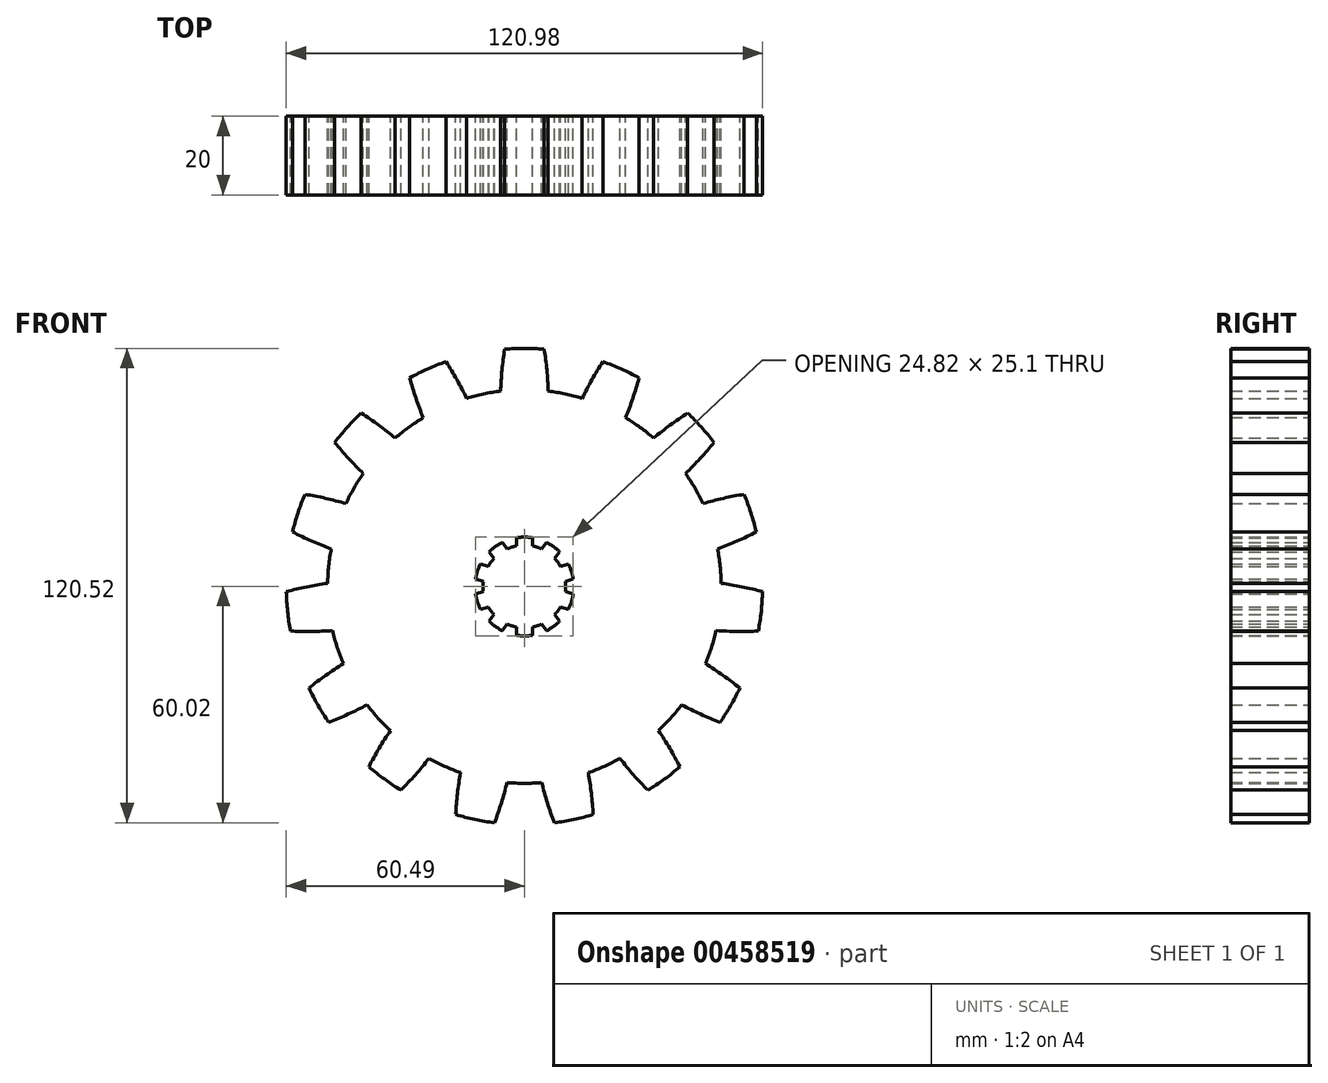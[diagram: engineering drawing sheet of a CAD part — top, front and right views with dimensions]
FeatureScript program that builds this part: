
annotation { "Feature Type Name" : "Feature", "Feature Type Description" : "" }
export const myFeature = defineFeature(function(context is Context, id is Id, definition is map)
    precondition{}
    {
        {
            var Q0;
            Q0=qCreatedBy(makeId("Front.planeOp"),FACE);
            var sketch = newSketch(context, id + "F0", { "sketchPlane" : qUnion([Q0])});
            skCircle(sketch, "E0", {"center": v(0, 0) * mm, "radius": 10.5 * mm});
            skLineSegment(sketch, "E1.left", {"start": v(2.05, -12.38) * mm, "end": v(2.05, -10.3) * mm});
            skLineSegment(sketch, "E1.right", {"start": v(-2.05, -12.38) * mm, "end": v(-2.05, -10.3) * mm});
            skLineSegment(sketch, "E2.1.0", {"start": v(8.94, -8.81) * mm, "end": v(7.71, -7.13) * mm});
            skLineSegment(sketch, "E2.1.1", {"start": v(5.62, -11.22) * mm, "end": v(4.4, -9.54) * mm});
            skLineSegment(sketch, "E2.2.0", {"start": v(12.4, -1.88) * mm, "end": v(10.43, -1.23) * mm});
            skLineSegment(sketch, "E2.2.1", {"start": v(11.14, -5.78) * mm, "end": v(9.16, -5.13) * mm});
            skLineSegment(sketch, "E2.3.0", {"start": v(11.14, 5.78) * mm, "end": v(9.16, 5.13) * mm});
            skLineSegment(sketch, "E2.3.1", {"start": v(12.4, 1.88) * mm, "end": v(10.43, 1.23) * mm});
            skLineSegment(sketch, "E2.4.0", {"start": v(5.62, 11.22) * mm, "end": v(4.4, 9.54) * mm});
            skLineSegment(sketch, "E2.4.1", {"start": v(8.94, 8.81) * mm, "end": v(7.71, 7.13) * mm});
            skLineSegment(sketch, "E2.5.0", {"start": v(-2.05, 12.38) * mm, "end": v(-2.05, 10.3) * mm});
            skLineSegment(sketch, "E2.5.1", {"start": v(2.05, 12.38) * mm, "end": v(2.05, 10.3) * mm});
            skLineSegment(sketch, "E2.6.0", {"start": v(-8.94, 8.81) * mm, "end": v(-7.71, 7.13) * mm});
            skLineSegment(sketch, "E2.6.1", {"start": v(-5.62, 11.22) * mm, "end": v(-4.4, 9.54) * mm});
            skLineSegment(sketch, "E2.7.0", {"start": v(-12.4, 1.88) * mm, "end": v(-10.43, 1.23) * mm});
            skLineSegment(sketch, "E2.7.1", {"start": v(-11.14, 5.78) * mm, "end": v(-9.16, 5.13) * mm});
            skLineSegment(sketch, "E2.8.0", {"start": v(-11.14, -5.78) * mm, "end": v(-9.16, -5.13) * mm});
            skLineSegment(sketch, "E2.9.0", {"start": v(-5.62, -11.22) * mm, "end": v(-4.4, -9.54) * mm});
            skLineSegment(sketch, "E2.9.1", {"start": v(-8.94, -8.81) * mm, "end": v(-7.71, -7.13) * mm});
            skLineSegment(sketch, "E3.trimOffspring", {"start": v(4.4, 9.54) * mm, "end": v(5.62, 11.22) * mm});
            skLineSegment(sketch, "E4.trimOffspring", {"start": v(2.05, 10.3) * mm, "end": v(2.05, 12.38) * mm});
            skLineSegment(sketch, "E5.trimOffspring", {"start": v(-4.4, 9.54) * mm, "end": v(-5.62, 11.22) * mm});
            skLineSegment(sketch, "E6.trimOffspring", {"start": v(-7.71, 7.13) * mm, "end": v(-8.94, 8.81) * mm});
            skLineSegment(sketch, "E7.trimOffspring", {"start": v(-10.43, 1.23) * mm, "end": v(-12.4, 1.88) * mm});
            skLineSegment(sketch, "E8.trimOffspring", {"start": v(-4.4, -9.54) * mm, "end": v(-5.62, -11.22) * mm});
            skLineSegment(sketch, "E9.trimOffspring", {"start": v(10.43, 1.23) * mm, "end": v(12.4, 1.88) * mm});
            skLineSegment(sketch, "E10.trimOffspring", {"start": v(9.16, 5.13) * mm, "end": v(11.14, 5.78) * mm});
            skLineSegment(sketch, "E11.trimOffspring", {"start": v(-2.05, 10.3) * mm, "end": v(-2.05, 12.38) * mm});
            skLineSegment(sketch, "E12.trimOffspring", {"start": v(-9.16, 5.13) * mm, "end": v(-11.14, 5.78) * mm});
            skLineSegment(sketch, "E13.trimOffspring", {"start": v(-10.43, -1.23) * mm, "end": v(-12.4, -1.88) * mm});
            skLineSegment(sketch, "E14.trimOffspring", {"start": v(-9.16, -5.13) * mm, "end": v(-11.14, -5.78) * mm});
            skLineSegment(sketch, "E15.trimOffspring", {"start": v(-7.71, -7.13) * mm, "end": v(-8.94, -8.81) * mm});
            skLineSegment(sketch, "E16.trimOffspring", {"start": v(-2.05, -10.3) * mm, "end": v(-2.05, -12.38) * mm});
            skLineSegment(sketch, "E17.trimOffspring", {"start": v(4.4, -9.54) * mm, "end": v(5.62, -11.22) * mm});
            skLineSegment(sketch, "E18.trimOffspring", {"start": v(7.71, 7.13) * mm, "end": v(8.94, 8.81) * mm});
            skLineSegment(sketch, "E19.trimOffspring", {"start": v(10.43, -1.23) * mm, "end": v(12.4, -1.88) * mm});
            skLineSegment(sketch, "E20.trimOffspring", {"start": v(9.16, -5.13) * mm, "end": v(11.14, -5.78) * mm});
            skLineSegment(sketch, "E21.trimOffspring", {"start": v(7.71, -7.13) * mm, "end": v(8.94, -8.81) * mm});
            skLineSegment(sketch, "E22.trimOffspring", {"start": v(2.05, -10.3) * mm, "end": v(2.05, -12.38) * mm});
            skArc(sketch, "E23", {"start": v(-5.62, 11.22) * mm, "mid": v(-7.38, 10.15) * mm, "end": v(-8.94, 8.81) * mm});
            skPoint(sketch, "E24.orphan", {"position": v(-2.05, 12.55) * mm});
            skPoint(sketch, "E25.orphan", {"position": v(2.05, 12.55) * mm});
            skPoint(sketch, "E26.orphan", {"position": v(-5.72, 11.36) * mm});
            skPoint(sketch, "E27.orphan", {"position": v(-9.04, 8.95) * mm});
            skPoint(sketch, "E28.orphan", {"position": v(5.72, 11.36) * mm});
            skPoint(sketch, "E29.orphan", {"position": v(9.04, 8.95) * mm});
            skPoint(sketch, "E30.orphan", {"position": v(11.3, 5.83) * mm});
            skPoint(sketch, "E31.orphan", {"position": v(12.57, 1.93) * mm});
            skPoint(sketch, "E32.orphan", {"position": v(12.57, -1.93) * mm});
            skPoint(sketch, "E33.orphan", {"position": v(11.3, -5.83) * mm});
            skPoint(sketch, "E34.orphan", {"position": v(9.04, -8.95) * mm});
            skPoint(sketch, "E35.orphan", {"position": v(5.72, -11.36) * mm});
            skPoint(sketch, "E36.orphan", {"position": v(2.05, -12.55) * mm});
            skPoint(sketch, "E37.orphan", {"position": v(-2.05, -12.55) * mm});
            skPoint(sketch, "E38.orphan", {"position": v(-5.72, -11.36) * mm});
            skPoint(sketch, "E39.orphan", {"position": v(-9.04, -8.95) * mm});
            skPoint(sketch, "E40.orphan", {"position": v(-11.3, -5.83) * mm});
            skPoint(sketch, "E41.orphan", {"position": v(-12.57, -1.93) * mm});
            skPoint(sketch, "E42.orphan", {"position": v(-12.57, 1.93) * mm});
            skPoint(sketch, "E43.orphan", {"position": v(-11.3, 5.83) * mm});
            skArc(sketch, "E44.trimOffspring", {"start": v(2.05, 12.38) * mm, "mid": v(0, 12.55) * mm, "end": v(-2.05, 12.38) * mm});
            skArc(sketch, "E45.trimOffspring", {"start": v(8.94, 8.81) * mm, "mid": v(7.38, 10.15) * mm, "end": v(5.62, 11.22) * mm});
            skArc(sketch, "E46.trimOffspring", {"start": v(-11.14, 5.78) * mm, "mid": v(-11.94, 3.88) * mm, "end": v(-12.4, 1.88) * mm});
            skArc(sketch, "E47.trimOffspring", {"start": v(-12.4, -1.88) * mm, "mid": v(-11.94, -3.88) * mm, "end": v(-11.14, -5.78) * mm});
            skArc(sketch, "E48.trimOffspring", {"start": v(-8.94, -8.81) * mm, "mid": v(-7.38, -10.15) * mm, "end": v(-5.62, -11.22) * mm});
            skArc(sketch, "E49.trimOffspring", {"start": v(-2.05, -12.38) * mm, "mid": v(0, -12.55) * mm, "end": v(2.05, -12.38) * mm});
            skArc(sketch, "E50.trimOffspring", {"start": v(5.62, -11.22) * mm, "mid": v(7.38, -10.15) * mm, "end": v(8.94, -8.81) * mm});
            skArc(sketch, "E51.trimOffspring", {"start": v(11.14, -5.78) * mm, "mid": v(11.94, -3.88) * mm, "end": v(12.4, -1.88) * mm});
            skArc(sketch, "E52.trimOffspring", {"start": v(12.4, 1.88) * mm, "mid": v(11.94, 3.88) * mm, "end": v(11.14, 5.78) * mm});
            skSolve(sketch);
        }
        {
            var Q0;
            Q0=qCreatedBy(makeId("Front.planeOp"),FACE);
            var sketch = newSketch(context, id + "F1", { "sketchPlane" : qUnion([Q0])});
            skCircle(sketch, "E53", {"center": v(0, 0) * mm, "radius": 50 * mm});
            skArc(sketch, "E54", {"start": v(-5.04, 60.29) * mm, "mid": v(-5.7, 54.98) * mm, "end": v(-6.05, 49.63) * mm});
            skArc(sketch, "E55.MirrorC", {"start": v(5.04, 60.29) * mm, "mid": v(5.7, 54.98) * mm, "end": v(6.05, 49.63) * mm});
            skArc(sketch, "E56.trimOffspring", {"start": v(5.04, 60.29) * mm, "mid": v(0, 60.5) * mm, "end": v(-5.04, 60.29) * mm});
            skArc(sketch, "E57.1.0", {"start": v(-29.12, 53.03) * mm, "mid": v(-27.57, 47.9) * mm, "end": v(-25.71, 42.88) * mm});
            skArc(sketch, "E57.1.1", {"start": v(-19.92, 57.13) * mm, "mid": v(-24.6, 55.27) * mm, "end": v(-29.12, 53.03) * mm});
            skArc(sketch, "E57.1.2", {"start": v(-19.92, 57.13) * mm, "mid": v(-17.15, 52.54) * mm, "end": v(-14.66, 47.8) * mm});
            skArc(sketch, "E57.2.0", {"start": v(-48.17, 36.6) * mm, "mid": v(-44.67, 32.55) * mm, "end": v(-40.93, 28.72) * mm});
            skArc(sketch, "E57.2.1", {"start": v(-41.43, 44.09) * mm, "mid": v(-44.96, 40.48) * mm, "end": v(-48.17, 36.6) * mm});
            skArc(sketch, "E57.2.2", {"start": v(-41.43, 44.09) * mm, "mid": v(-37.04, 41.02) * mm, "end": v(-32.84, 37.7) * mm});
            skArc(sketch, "E58.3.3.0", {"start": v(-58.9, 13.84) * mm, "mid": v(-54.05, 11.57) * mm, "end": v(-49.07, 9.59) * mm});
            skArc(sketch, "E58.4.3.0", {"start": v(-55.78, 23.42) * mm, "mid": v(-57.54, 18.7) * mm, "end": v(-58.9, 13.84) * mm});
            skArc(sketch, "E58.8.3.0", {"start": v(-55.78, 23.42) * mm, "mid": v(-50.52, 22.4) * mm, "end": v(-45.34, 21.09) * mm});
            skArc(sketch, "E58.3.4.0", {"start": v(-59.43, -11.31) * mm, "mid": v(-54.08, -11.42) * mm, "end": v(-48.73, -11.2) * mm});
            skArc(sketch, "E58.4.4.0", {"start": v(-60.49, -1.3) * mm, "mid": v(-60.17, -6.32) * mm, "end": v(-59.43, -11.31) * mm});
            skArc(sketch, "E58.8.4.0", {"start": v(-60.49, -1.3) * mm, "mid": v(-55.27, -0.08) * mm, "end": v(-50, 0.82) * mm});
            skArc(sketch, "E58.3.5.0", {"start": v(-49.7, -34.5) * mm, "mid": v(-44.76, -32.42) * mm, "end": v(-39.96, -30.05) * mm});
            skArc(sketch, "E58.4.5.0", {"start": v(-54.73, -25.78) * mm, "mid": v(-52.4, -30.25) * mm, "end": v(-49.7, -34.5) * mm});
            skArc(sketch, "E58.8.5.0", {"start": v(-54.73, -25.78) * mm, "mid": v(-50.46, -22.55) * mm, "end": v(-46, -19.58) * mm});
            skArc(sketch, "E58.3.6.0", {"start": v(-31.36, -51.74) * mm, "mid": v(-27.7, -47.83) * mm, "end": v(-24.28, -43.7) * mm});
            skArc(sketch, "E58.4.6.0", {"start": v(-39.51, -45.81) * mm, "mid": v(-35.56, -48.95) * mm, "end": v(-31.36, -51.74) * mm});
            skArc(sketch, "E58.8.6.0", {"start": v(-39.51, -45.81) * mm, "mid": v(-36.93, -41.13) * mm, "end": v(-34.06, -36.6) * mm});
            skArc(sketch, "E58.3.7.0", {"start": v(-7.6, -60.02) * mm, "mid": v(-5.85, -54.96) * mm, "end": v(-4.4, -49.8) * mm});
            skArc(sketch, "E58.4.7.0", {"start": v(-17.46, -57.93) * mm, "mid": v(-12.58, -59.18) * mm, "end": v(-7.6, -60.02) * mm});
            skArc(sketch, "E58.8.7.0", {"start": v(-17.46, -57.93) * mm, "mid": v(-17, -52.6) * mm, "end": v(-16.23, -47.3) * mm});
            skArc(sketch, "E58.3.8.0", {"start": v(17.46, -57.93) * mm, "mid": v(17, -52.6) * mm, "end": v(16.23, -47.3) * mm});
            skArc(sketch, "E58.4.8.0", {"start": v(7.6, -60.02) * mm, "mid": v(12.58, -59.18) * mm, "end": v(17.46, -57.93) * mm});
            skArc(sketch, "E58.8.8.0", {"start": v(7.6, -60.02) * mm, "mid": v(5.85, -54.96) * mm, "end": v(4.4, -49.8) * mm});
            skArc(sketch, "E58.3.9.0", {"start": v(39.51, -45.81) * mm, "mid": v(36.93, -41.13) * mm, "end": v(34.06, -36.6) * mm});
            skArc(sketch, "E58.4.9.0", {"start": v(31.36, -51.74) * mm, "mid": v(35.56, -48.95) * mm, "end": v(39.51, -45.81) * mm});
            skArc(sketch, "E58.8.9.0", {"start": v(31.36, -51.74) * mm, "mid": v(27.7, -47.83) * mm, "end": v(24.28, -43.7) * mm});
            skArc(sketch, "E58.3.10.0", {"start": v(54.73, -25.78) * mm, "mid": v(50.46, -22.55) * mm, "end": v(46, -19.58) * mm});
            skArc(sketch, "E58.4.10.0", {"start": v(49.7, -34.5) * mm, "mid": v(52.4, -30.25) * mm, "end": v(54.73, -25.78) * mm});
            skArc(sketch, "E58.8.10.0", {"start": v(49.7, -34.5) * mm, "mid": v(44.76, -32.42) * mm, "end": v(39.96, -30.05) * mm});
            skArc(sketch, "E58.3.11.0", {"start": v(60.49, -1.3) * mm, "mid": v(55.27, -0.08) * mm, "end": v(50, 0.82) * mm});
            skArc(sketch, "E58.4.11.0", {"start": v(59.43, -11.31) * mm, "mid": v(60.17, -6.32) * mm, "end": v(60.49, -1.3) * mm});
            skArc(sketch, "E58.8.11.0", {"start": v(59.43, -11.31) * mm, "mid": v(54.08, -11.42) * mm, "end": v(48.73, -11.2) * mm});
            skArc(sketch, "E58.3.12.0", {"start": v(55.78, 23.42) * mm, "mid": v(50.52, 22.4) * mm, "end": v(45.34, 21.09) * mm});
            skArc(sketch, "E58.4.12.0", {"start": v(58.9, 13.84) * mm, "mid": v(57.54, 18.7) * mm, "end": v(55.78, 23.42) * mm});
            skArc(sketch, "E58.8.12.0", {"start": v(58.9, 13.84) * mm, "mid": v(54.05, 11.57) * mm, "end": v(49.07, 9.59) * mm});
            skArc(sketch, "E58.3.13.0", {"start": v(41.43, 44.09) * mm, "mid": v(37.04, 41.02) * mm, "end": v(32.84, 37.7) * mm});
            skArc(sketch, "E58.4.13.0", {"start": v(48.17, 36.6) * mm, "mid": v(44.96, 40.48) * mm, "end": v(41.43, 44.09) * mm});
            skArc(sketch, "E58.8.13.0", {"start": v(48.17, 36.6) * mm, "mid": v(44.67, 32.55) * mm, "end": v(40.93, 28.72) * mm});
            skArc(sketch, "E58.3.14.0", {"start": v(19.92, 57.13) * mm, "mid": v(17.15, 52.54) * mm, "end": v(14.66, 47.8) * mm});
            skArc(sketch, "E58.4.14.0", {"start": v(29.12, 53.03) * mm, "mid": v(24.6, 55.27) * mm, "end": v(19.92, 57.13) * mm});
            skArc(sketch, "E58.8.14.0", {"start": v(29.12, 53.03) * mm, "mid": v(27.57, 47.9) * mm, "end": v(25.71, 42.88) * mm});
            skSolve(sketch);
        }
        {
            var Q0;
            {var subQ0=sQuery(id+"F1.wireOp",EDGE,"E54");Q0=makeQuery(id+"F1.imprint","IMPRINT",FACE,{"disambiguationData":[TD([[makeQuery(id+"F1.imprint","IMPRINT",EDGE,{"derivedFrom":subQ0}),1.0]])]});}
            var Q1;
            {var subQ0=sQuery(id+"F1.wireOp",EDGE,"E58.3.14.0");Q1=makeQuery(id+"F1.imprint","IMPRINT",FACE,{"disambiguationData":[TD([[makeQuery(id+"F1.imprint","IMPRINT",EDGE,{"derivedFrom":subQ0}),1.0]])]});}
            var Q2;
            {var subQ0=sQuery(id+"F1.wireOp",EDGE,"E58.3.13.0");Q2=makeQuery(id+"F1.imprint","IMPRINT",FACE,{"disambiguationData":[TD([[makeQuery(id+"F1.imprint","IMPRINT",EDGE,{"derivedFrom":subQ0}),1.0]])]});}
            var Q3;
            {var subQ0=sQuery(id+"F1.wireOp",EDGE,"E58.3.12.0");Q3=makeQuery(id+"F1.imprint","IMPRINT",FACE,{"disambiguationData":[TD([[makeQuery(id+"F1.imprint","IMPRINT",EDGE,{"derivedFrom":subQ0}),1.0]])]});}
            var Q4;
            {var subQ0=sQuery(id+"F1.wireOp",EDGE,"E58.3.11.0");Q4=makeQuery(id+"F1.imprint","IMPRINT",FACE,{"disambiguationData":[TD([[makeQuery(id+"F1.imprint","IMPRINT",EDGE,{"derivedFrom":subQ0}),1.0]])]});}
            var Q5;
            {var subQ0=sQuery(id+"F1.wireOp",EDGE,"E58.3.10.0");Q5=makeQuery(id+"F1.imprint","IMPRINT",FACE,{"disambiguationData":[TD([[makeQuery(id+"F1.imprint","IMPRINT",EDGE,{"derivedFrom":subQ0}),1.0]])]});}
            var Q6;
            {var subQ0=sQuery(id+"F1.wireOp",EDGE,"E58.3.9.0");Q6=makeQuery(id+"F1.imprint","IMPRINT",FACE,{"disambiguationData":[TD([[makeQuery(id+"F1.imprint","IMPRINT",EDGE,{"derivedFrom":subQ0}),1.0]])]});}
            var Q7;
            {var subQ0=sQuery(id+"F1.wireOp",EDGE,"E58.3.8.0");Q7=makeQuery(id+"F1.imprint","IMPRINT",FACE,{"disambiguationData":[TD([[makeQuery(id+"F1.imprint","IMPRINT",EDGE,{"derivedFrom":subQ0}),1.0]])]});}
            var Q8;
            {var subQ0=sQuery(id+"F1.wireOp",EDGE,"E58.3.7.0");Q8=makeQuery(id+"F1.imprint","IMPRINT",FACE,{"disambiguationData":[TD([[makeQuery(id+"F1.imprint","IMPRINT",EDGE,{"derivedFrom":subQ0}),1.0]])]});}
            var Q9;
            {var subQ0=sQuery(id+"F1.wireOp",EDGE,"E58.3.6.0");Q9=makeQuery(id+"F1.imprint","IMPRINT",FACE,{"disambiguationData":[TD([[makeQuery(id+"F1.imprint","IMPRINT",EDGE,{"derivedFrom":subQ0}),1.0]])]});}
            var Q10;
            {var subQ0=sQuery(id+"F1.wireOp",EDGE,"E58.3.5.0");Q10=makeQuery(id+"F1.imprint","IMPRINT",FACE,{"disambiguationData":[TD([[makeQuery(id+"F1.imprint","IMPRINT",EDGE,{"derivedFrom":subQ0}),1.0]])]});}
            var Q11;
            {var subQ0=sQuery(id+"F1.wireOp",EDGE,"E58.3.4.0");Q11=makeQuery(id+"F1.imprint","IMPRINT",FACE,{"disambiguationData":[TD([[makeQuery(id+"F1.imprint","IMPRINT",EDGE,{"derivedFrom":subQ0}),1.0]])]});}
            var Q12;
            {var subQ0=sQuery(id+"F1.wireOp",EDGE,"E58.3.3.0");Q12=makeQuery(id+"F1.imprint","IMPRINT",FACE,{"disambiguationData":[TD([[makeQuery(id+"F1.imprint","IMPRINT",EDGE,{"derivedFrom":subQ0}),1.0]])]});}
            var Q13;
            {var subQ0=sQuery(id+"F1.wireOp",EDGE,"E57.1.0");Q13=makeQuery(id+"F1.imprint","IMPRINT",FACE,{"disambiguationData":[TD([[makeQuery(id+"F1.imprint","IMPRINT",EDGE,{"derivedFrom":subQ0}),1.0]])]});}
            var Q14;
            {var subQ0=sQuery(id+"F1.wireOp",EDGE,"E53");var subQ18=makeQuery(id+"F1.imprint","INTERSECT",VERTEX,{"derivedFrom":[subQ0,sQuery(id+"F1.wireOp",EDGE,"E58.3.11.0")]});Q14=makeQuery(id+"F1.imprint","IMPRINT",FACE,{"disambiguationData":[TD([[makeQuery(id+"F1.imprint","IMPRINT",EDGE,{"disambiguationData":[TD([[subQ18,-1.0]])],"derivedFrom":subQ0}),1.0]])]});}
            var Q15;
            {var subQ0=sQuery(id+"F1.wireOp",EDGE,"E57.2.0");Q15=makeQuery(id+"F1.imprint","IMPRINT",FACE,{"disambiguationData":[TD([[makeQuery(id+"F1.imprint","IMPRINT",EDGE,{"derivedFrom":subQ0}),1.0]])]});}
            extrude(context, id + "F2", {"entities" : qUnion([Q0, Q1, Q2, Q3, Q4, Q5, Q6, Q7, Q8, Q9, Q10, Q11, Q12, Q13, Q14, Q15]), "depth" : 20 * mm, "offsetDistance" : 25 * mm, "symmetric" : true});
        }
        {
            var Q0;
            Q0 = qSketchRegion(id + "F0", true);
            var Q1;
            Q1=sQuery(id+"F0.wireOp",EDGE,"E0");
            var Q2;
            Q2=sQuery(id+"F0.wireOp",EDGE,"E44.trimOffspring");
            var Q3;
            Q3=sQuery(id+"F0.wireOp",EDGE,"E2.5.0");
            var Q4;
            Q4=sQuery(id+"F0.wireOp",EDGE,"E2.5.1");
            var Q5;
            Q5=sQuery(id+"F0.wireOp",EDGE,"E2.4.0");
            var Q6;
            Q6=sQuery(id+"F0.wireOp",EDGE,"E45.trimOffspring");
            var Q7;
            Q7=sQuery(id+"F0.wireOp",EDGE,"E2.4.1");
            var Q8;
            Q8=sQuery(id+"F0.wireOp",EDGE,"E2.3.0");
            var Q9;
            Q9=sQuery(id+"F0.wireOp",EDGE,"E2.3.1");
            var Q10;
            Q10=sQuery(id+"F0.wireOp",EDGE,"E52.trimOffspring");
            var Q11;
            Q11=sQuery(id+"F0.wireOp",EDGE,"E2.2.0");
            var Q12;
            Q12=sQuery(id+"F0.wireOp",EDGE,"E51.trimOffspring");
            var Q13;
            Q13=sQuery(id+"F0.wireOp",EDGE,"E2.2.1");
            var Q14;
            Q14=sQuery(id+"F0.wireOp",EDGE,"E2.1.0");
            var Q15;
            Q15=sQuery(id+"F0.wireOp",EDGE,"E50.trimOffspring");
            var Q16;
            Q16=sQuery(id+"F0.wireOp",EDGE,"E2.1.1");
            var Q17;
            Q17=sQuery(id+"F0.wireOp",EDGE,"E22.trimOffspring");
            var Q18;
            Q18=sQuery(id+"F0.wireOp",EDGE,"E49.trimOffspring");
            var Q19;
            Q19=sQuery(id+"F0.wireOp",EDGE,"E8.trimOffspring");
            var Q20;
            Q20=sQuery(id+"F0.wireOp",EDGE,"E48.trimOffspring");
            var Q21;
            Q21=sQuery(id+"F0.wireOp",EDGE,"E2.9.1");
            var Q22;
            Q22=sQuery(id+"F0.wireOp",EDGE,"E2.8.0");
            var Q23;
            Q23=sQuery(id+"F0.wireOp",EDGE,"E47.trimOffspring");
            var Q24;
            Q24=sQuery(id+"F0.wireOp",EDGE,"E7.trimOffspring");
            var Q25;
            Q25=sQuery(id+"F0.wireOp",EDGE,"E46.trimOffspring");
            var Q26;
            Q26=sQuery(id+"F0.wireOp",EDGE,"E13.trimOffspring");
            var Q27;
            Q27=sQuery(id+"F0.wireOp",EDGE,"E2.6.0");
            var Q28;
            Q28=sQuery(id+"F0.wireOp",EDGE,"E23");
            var Q29;
            Q29=sQuery(id+"F0.wireOp",EDGE,"E5.trimOffspring");
            var Q30;
            Q30=sQuery(id+"F0.wireOp",EDGE,"E12.trimOffspring");
            extrude(context, id + "F3", {"entities" : qUnion([Q0]), "operationType" : NewBodyOperationType.REMOVE, "surfaceEntities" : qUnion([Q1, Q2, Q3, Q4, Q5, Q6, Q7, Q8, Q9, Q10, Q11, Q12, Q13, Q14, Q15, Q16, Q17, Q18, Q19, Q20, Q21, Q22, Q23, Q24, Q25, Q26, Q27, Q28, Q29, Q30]), "depth" : 25 * mm, "offsetDistance" : 25 * mm, "symmetric" : true});
        }
    });
